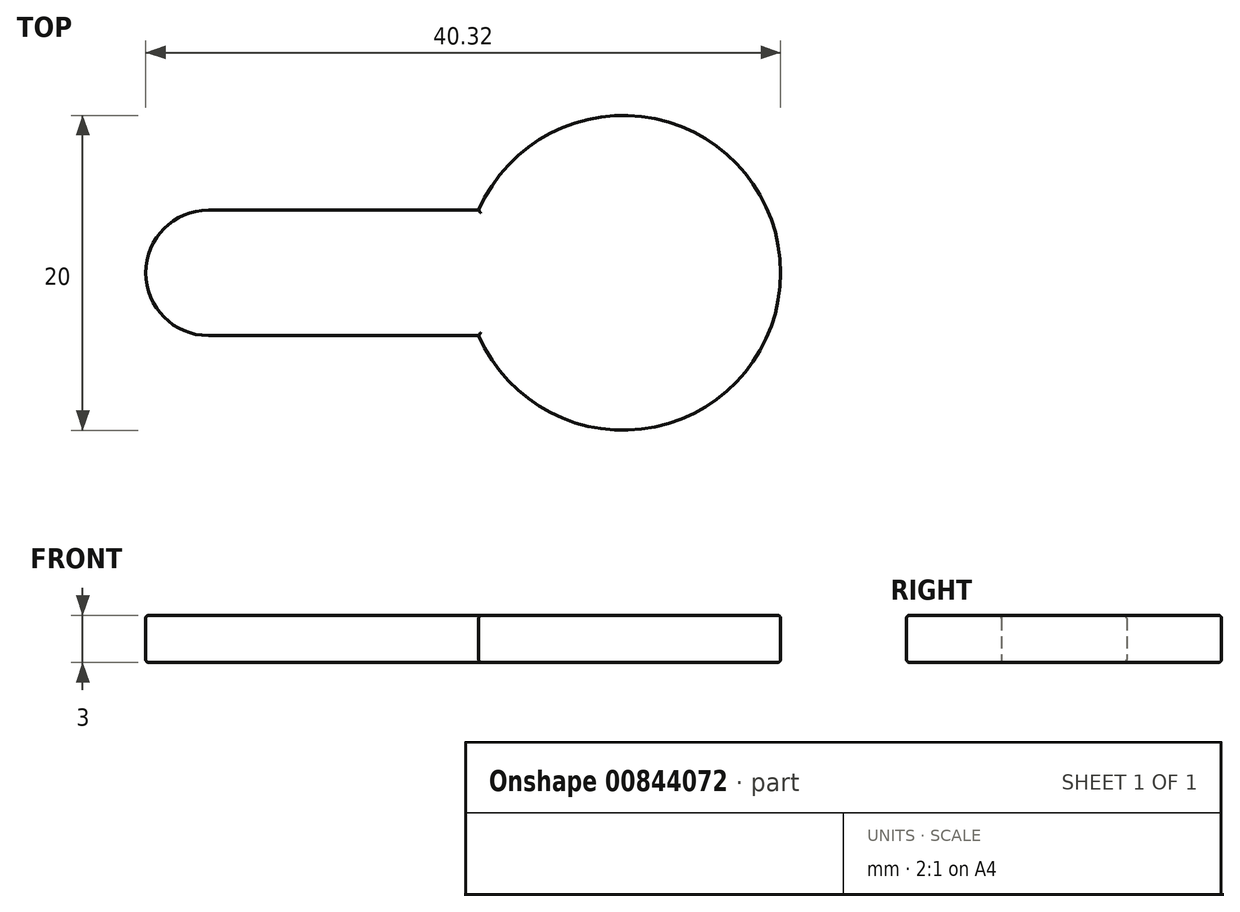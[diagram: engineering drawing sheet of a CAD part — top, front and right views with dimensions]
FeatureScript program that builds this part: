
annotation { "Feature Type Name" : "Feature", "Feature Type Description" : "" }
export const myFeature = defineFeature(function(context is Context, id is Id, definition is map)
    precondition{}
    {
        {
            var Q0;
            Q0=qCreatedBy(makeId("Top.planeOp"),FACE);
            var sketch = newSketch(context, id + "F0", { "sketchPlane" : qUnion([Q0])});
            skCircle(sketch, "E0", {"center": v(0, 0) * mm, "radius": 10 * mm});
            skLineSegment(sketch, "E1", {"start": v(0, 0) * mm, "end": v(-30.32, 0) * mm, "construction": true});
            skCircle(sketch, "E2", {"center": v(-26.34, 0) * mm, "radius": 3.99 * mm});
            skLineSegment(sketch, "E3", {"start": v(-26.34, 3.99) * mm, "end": v(-9.17, 3.99) * mm});
            skLineSegment(sketch, "E4.MirrorCS", {"start": v(-26.34, -3.99) * mm, "end": v(-9.17, -3.99) * mm});
            skSolve(sketch);
        }
        {
            var Q0;
            {var subQ0=sQuery(id+"F0.wireOp",EDGE,"E0");var subQ1=makeQuery(id+"F0.imprint","INTERSECT",VERTEX,{"derivedFrom":[subQ0,sQuery(id+"F0.wireOp",EDGE,"E3")]});Q0=makeQuery(id+"F0.imprint","IMPRINT",FACE,{"disambiguationData":[TD([[makeQuery(id+"F0.imprint","IMPRINT",EDGE,{"disambiguationData":[TD([[subQ1,-1.0]])],"derivedFrom":subQ0}),1.0]])]});}
            var Q1;
            {var subQ0=sQuery(id+"F0.wireOp",EDGE,"E3");Q1=makeQuery(id+"F0.imprint","IMPRINT",FACE,{"disambiguationData":[TD([[makeQuery(id+"F0.imprint","IMPRINT",EDGE,{"derivedFrom":subQ0}),-1.0]])]});}
            var Q2;
            {var subQ0=sQuery(id+"F0.wireOp",EDGE,"E2");var subQ1=makeQuery(id+"F0.imprint","INTERSECT",VERTEX,{"derivedFrom":[subQ0,sQuery(id+"F0.wireOp",EDGE,"E3")]});Q2=makeQuery(id+"F0.imprint","IMPRINT",FACE,{"disambiguationData":[TD([[makeQuery(id+"F0.imprint","IMPRINT",EDGE,{"disambiguationData":[TD([[subQ1,-1.0]])],"derivedFrom":subQ0}),1.0]])]});}
            extrude(context, id + "F1", {"entities" : qUnion([Q0, Q1, Q2]), "depth" : 3 * mm, "offsetDistance" : 25 * mm});
        }
        {
            var Q0;
            Q0=makeQuery(id+"F1.opExtrude","CAP_FACE",FACE,{"disambiguationData":[OSD([sQuery(id+"F0.wireOp",EDGE,"E0"),sQuery(id+"F0.wireOp",EDGE,"E2"),sQuery(id+"F0.wireOp",EDGE,"E3"),sQuery(id+"F0.wireOp",EDGE,"E4.MirrorCS")])],"isStart":false});
            var Q1;
            Q1=makeQuery(id+"F1.opExtrude","CAP_FACE",FACE,{"disambiguationData":[OSD([sQuery(id+"F0.wireOp",EDGE,"E0"),sQuery(id+"F0.wireOp",EDGE,"E2"),sQuery(id+"F0.wireOp",EDGE,"E3"),sQuery(id+"F0.wireOp",EDGE,"E4.MirrorCS")])],"isStart":true});
            fillet(context, id + "F2", {"entities" : qUnion([Q0, Q1]), "radius" : .2 * mm, "tangentPropagation" : true, "allowEdgeOverflow" : false});
        }
    });
